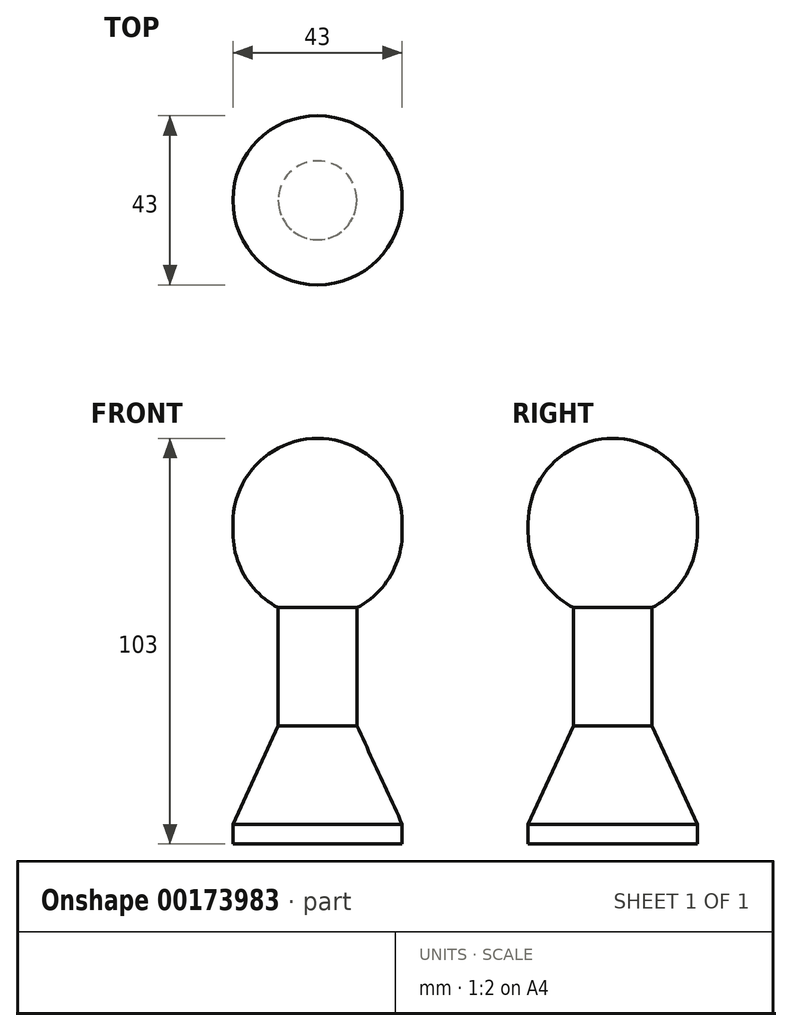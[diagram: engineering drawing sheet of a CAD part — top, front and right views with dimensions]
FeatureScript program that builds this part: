
annotation { "Feature Type Name" : "Feature", "Feature Type Description" : "" }
export const myFeature = defineFeature(function(context is Context, id is Id, definition is map)
    precondition{}
    {
        {
            var Q0;
            Q0=qCreatedBy(makeId("Top.planeOp"),FACE);
            var sketch = newSketch(context, id + "F0", { "sketchPlane" : qUnion([Q0])});
            skCircle(sketch, "E0", {"center": v(0, 0) * mm, "radius": 21.5 * mm});
            skSolve(sketch);
        }
        {
            var Q0;
            Q0=makeQuery(id+"F0.imprint","IMPRINT",FACE,{"disambiguationData":[TD([[makeQuery(id+"F0.imprint","IMPRINT",EDGE,{"derivedFrom":sQuery(id+"F0.wireOp",EDGE,"E0")}),1.0]])]});
            extrude(context, id + "F1", {"entities" : qUnion([Q0]), "depth" : 30 * mm});
        }
        {
            var Q0;
            Q0=makeQuery(id+"F1.opExtrude","CAP_EDGE",EDGE,{"disambiguationData":[OSD([sQuery(id+"F0.wireOp",EDGE,"E0")])],"isStart":false});
            chamfer(context, id + "F2", {"entities" : qUnion([Q0]), "chamferType" : ChamferType.TWO_OFFSETS, "width1" : ((43 / 2) - 10) * mm, "oppositeDirection" : false, "width2" : 25 * mm, "tangentPropagation" : true});
        }
        {
            var Q0;
            Q0=makeQuery(id+"F1.opExtrude","CAP_FACE",FACE,{"disambiguationData":[OSD([sQuery(id+"F0.wireOp",EDGE,"E0")])],"isStart":false});
            extrude(context, id + "F3", {"entities" : qUnion([Q0]), "operationType" : NewBodyOperationType.ADD, "depth" : 30 * mm});
        }
        {
            var Q0;
            Q0=makeQuery(id+"F3.opExtrude","CAP_FACE",FACE,{"disambiguationData":[OSD([sQuery(id+"F0.wireOp",EDGE,"E0")])],"isStart":false});
            var sketch = newSketch(context, id + "F4", { "sketchPlane" : qUnion([Q0])});
            skCircle(sketch, "E1", {"center": v(0, 0) * mm, "radius": 21.5 * mm});
            skSolve(sketch);
        }
        {
            var Q0;
            Q0 = qSketchRegion(id + "F4", true);
            extrude(context, id + "F5", {"entities" : qUnion([Q0]), "operationType" : NewBodyOperationType.ADD, "depth" : 43 * mm});
        }
        {
            var Q0;
            Q0=makeQuery(id+"F5.opExtrude","CAP_EDGE",EDGE,{"disambiguationData":[OSD([sQuery(id+"F4.wireOp",EDGE,"E1")])],"isStart":false});
            var Q1;
            Q1=makeQuery(id+"F5.opExtrude","CAP_EDGE",EDGE,{"disambiguationData":[OSD([sQuery(id+"F4.wireOp",EDGE,"E1")])],"isStart":true});
            fillet(context, id + "F6", {"entities" : qUnion([Q0, Q1]), "radius" : ((43 / 2) - 0) * mm, "tangentPropagation" : true, "allowEdgeOverflow" : false});
        }
    });
